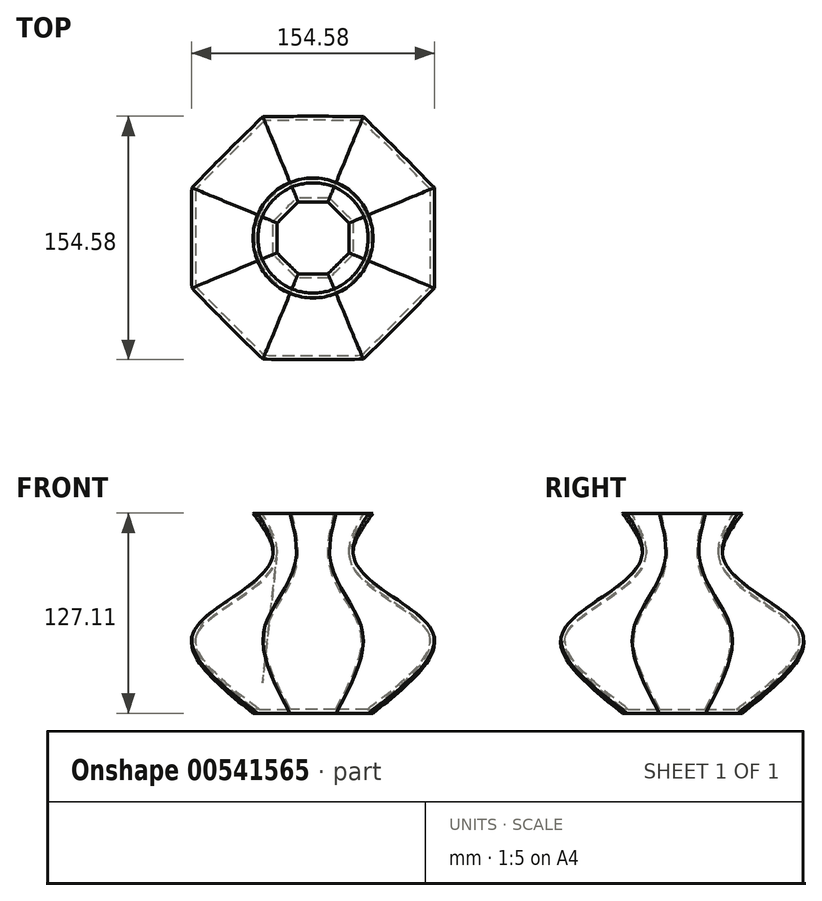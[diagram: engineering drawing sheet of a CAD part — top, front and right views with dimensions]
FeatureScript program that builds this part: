
annotation { "Feature Type Name" : "Feature", "Feature Type Description" : "" }
export const myFeature = defineFeature(function(context is Context, id is Id, definition is map)
    precondition{}
    {
        {
            var Q0;
            Q0=qCreatedBy(makeId("Top.planeOp"),FACE);
            var sketch = newSketch(context, id + "F0", { "sketchPlane" : qUnion([Q0])});
            skCircle(sketch, "E0", {"center": v(0, 0) * mm, "radius": 38.1 * mm});
            skSolve(sketch);
        }
        {
            var Q0;
            Q0=qCreatedBy(makeId("Top.planeOp"),FACE);
            cPlane(context, id + "F1", {"entities" : qUnion([Q0]), "cplaneType" : CPlaneType.OFFSET, "offset" : 50.8 * mm, "width" : 152.4 * mm, "height" : 152.4 * mm});
        }
        {
            var Q0;
            Q0=qCreatedBy(id+"F1.planeOp",FACE);
            var sketch = newSketch(context, id + "F2", { "sketchPlane" : qUnion([Q0])});
            skCircle(sketch, "E1.cCircle", {"center": v(0, 0) * mm, "radius": 76.2 * mm, "construction": true});
            skLineSegment(sketch, "E1.0", {"start": v(-31.56, 76.2) * mm, "end": v(31.56, 76.2) * mm});
            skLineSegment(sketch, "E1.1", {"start": v(31.56, 76.2) * mm, "end": v(76.2, 31.56) * mm});
            skLineSegment(sketch, "E1.2", {"start": v(76.2, 31.56) * mm, "end": v(76.2, -31.56) * mm});
            skLineSegment(sketch, "E1.3", {"start": v(76.2, -31.56) * mm, "end": v(31.56, -76.2) * mm});
            skLineSegment(sketch, "E1.4", {"start": v(31.56, -76.2) * mm, "end": v(-31.56, -76.2) * mm});
            skLineSegment(sketch, "E1.5", {"start": v(-31.56, -76.2) * mm, "end": v(-76.2, -31.56) * mm});
            skLineSegment(sketch, "E1.6", {"start": v(-76.2, -31.56) * mm, "end": v(-76.2, 31.56) * mm});
            skLineSegment(sketch, "E1.7", {"start": v(-76.2, 31.56) * mm, "end": v(-31.56, 76.2) * mm});
            skPoint(sketch, "E1.0.midPoint", {"position": v(0, 76.2) * mm});
            skSolve(sketch);
        }
        {
            var Q0;
            Q0=qCreatedBy(id+"F1.planeOp",FACE);
            cPlane(context, id + "F3", {"entities" : qUnion([Q0]), "cplaneType" : CPlaneType.OFFSET, "offset" : 50.8 * mm, "width" : 152.4 * mm, "height" : 152.4 * mm});
        }
        {
            var Q0;
            Q0=qCreatedBy(id+"F3.planeOp",FACE);
            var sketch = newSketch(context, id + "F4", { "sketchPlane" : qUnion([Q0])});
            skCircle(sketch, "E2.cCircle", {"center": v(0, 0) * mm, "radius": 25.4 * mm, "construction": true});
            skLineSegment(sketch, "E2.0", {"start": v(-10.52, 25.4) * mm, "end": v(10.52, 25.4) * mm});
            skLineSegment(sketch, "E2.1", {"start": v(10.52, 25.4) * mm, "end": v(25.4, 10.52) * mm});
            skLineSegment(sketch, "E2.2", {"start": v(25.4, 10.52) * mm, "end": v(25.4, -10.52) * mm});
            skLineSegment(sketch, "E2.3", {"start": v(25.4, -10.52) * mm, "end": v(10.52, -25.4) * mm});
            skLineSegment(sketch, "E2.4", {"start": v(10.52, -25.4) * mm, "end": v(-10.52, -25.4) * mm});
            skLineSegment(sketch, "E2.5", {"start": v(-10.52, -25.4) * mm, "end": v(-25.4, -10.52) * mm});
            skLineSegment(sketch, "E2.6", {"start": v(-25.4, -10.52) * mm, "end": v(-25.4, 10.52) * mm});
            skLineSegment(sketch, "E2.7", {"start": v(-25.4, 10.52) * mm, "end": v(-10.52, 25.4) * mm});
            skPoint(sketch, "E2.0.midPoint", {"position": v(0, 25.4) * mm});
            skSolve(sketch);
        }
        {
            var Q0;
            Q0=qCreatedBy(id+"F3.planeOp",FACE);
            cPlane(context, id + "F5", {"entities" : qUnion([Q0]), "cplaneType" : CPlaneType.OFFSET, "offset" : 25.4 * mm, "width" : 152.4 * mm, "height" : 152.4 * mm});
        }
        {
            var Q0;
            Q0=qCreatedBy(id+"F5.planeOp",FACE);
            var sketch = newSketch(context, id + "F6", { "sketchPlane" : qUnion([Q0])});
            skCircle(sketch, "E3", {"center": v(0, 0) * mm, "radius": 38.1 * mm});
            skSolve(sketch);
        }
        {
            var Q0;
            Q0=makeQuery(id+"F0.imprint","IMPRINT",FACE,{"disambiguationData":[TD([[makeQuery(id+"F0.imprint","IMPRINT",EDGE,{"derivedFrom":sQuery(id+"F0.wireOp",EDGE,"E0")}),1.0]])]});
            var Q1;
            Q1=makeQuery(id+"F2.imprint","IMPRINT",FACE,{"disambiguationData":[TD([[makeQuery(id+"F2.imprint","IMPRINT",EDGE,{"derivedFrom":sQuery(id+"F2.wireOp",EDGE,"E1.0")}),-1.0]])]});
            var Q2;
            Q2=makeQuery(id+"F4.imprint","IMPRINT",FACE,{"disambiguationData":[TD([[makeQuery(id+"F4.imprint","IMPRINT",EDGE,{"derivedFrom":sQuery(id+"F4.wireOp",EDGE,"E2.0")}),-1.0]])]});
            var Q3;
            Q3=makeQuery(id+"F6.imprint","IMPRINT",FACE,{"disambiguationData":[TD([[makeQuery(id+"F6.imprint","IMPRINT",EDGE,{"derivedFrom":sQuery(id+"F6.wireOp",EDGE,"E3")}),1.0]])]});
            loft(context, id + "F7", {"sheetProfilesArray" : [{ "sheetProfileEntities" : qUnion([Q0]) }, { "sheetProfileEntities" : qUnion([Q1]) }, { "sheetProfileEntities" : qUnion([Q2]) }, { "sheetProfileEntities" : qUnion([Q3]) }]});
        }
        {
            var Q0;
            Q0=makeQuery(id+"F7.opLoft","CAP_FACE",FACE,{"disambiguationData":[OSD([makeQuery(id+"F6.imprint","IMPRINT",FACE,{"disambiguationData":[TD([[makeQuery(id+"F6.imprint","IMPRINT",EDGE,{"derivedFrom":sQuery(id+"F6.wireOp",EDGE,"E3")}),1.0]])]})])],"isStart":true});
            shell(context, id + "F8", {"entities" : qUnion([Q0]), "thickness" : 2.54 * mm});
        }
    });
